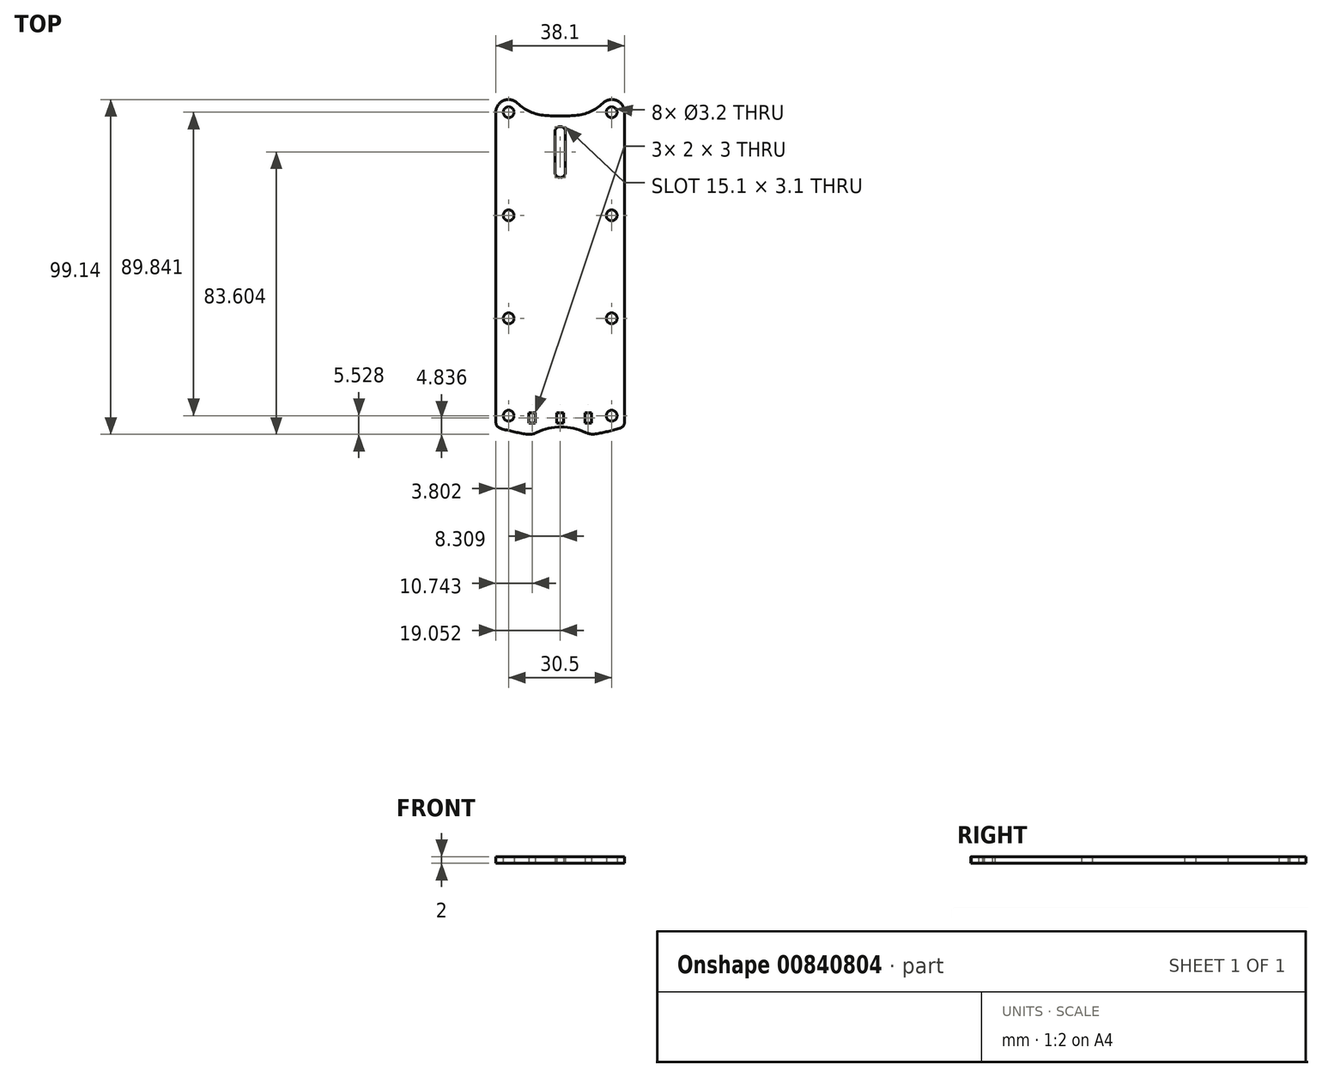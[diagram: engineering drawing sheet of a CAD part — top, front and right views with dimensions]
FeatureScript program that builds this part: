
annotation { "Feature Type Name" : "Feature", "Feature Type Description" : "" }
export const myFeature = defineFeature(function(context is Context, id is Id, definition is map)
    precondition{}
    {
        {
            var Q0;
            Q0=qCreatedBy(makeId("Top.planeOp"),FACE);
            var sketch = newSketch(context, id + "F0", { "sketchPlane" : qUnion([Q0])});
            skPoint(sketch, "E0.middle", {"position": v(-26.8, 6.98) * mm});
            skPoint(sketch, "E1.middle", {"position": v(-26.8, 51) * mm});
            skPoint(sketch, "E1.centerSnap0", {"position": v(-26.8, 26.98) * mm});
            skLineSegment(sketch, "E2.0", {"start": v(-45.86, 66.25) * mm, "end": v(-45.86, 60.43) * mm});
            skLineSegment(sketch, "E3", {"start": v(-7.76, 35.75) * mm, "end": v(-7.76, 5.25) * mm});
            skLineSegment(sketch, "E4.left", {"start": v(-45.86, 60.43) * mm, "end": v(-45.86, 5.25) * mm});
            skCircle(sketch, "E5", {"center": v(-11.56, 66.25) * mm, "radius": 1.6 * mm});
            skCircle(sketch, "E6", {"center": v(-42.06, 66.25) * mm, "radius": 1.6 * mm});
            skCircle(sketch, "E7", {"center": v(-42.06, 35.75) * mm, "radius": 1.6 * mm});
            skCircle(sketch, "E8", {"center": v(-11.56, 35.75) * mm, "radius": 1.6 * mm});
            skArc(sketch, "E9", {"start": v(-38.3, 66.25) * mm, "mid": v(-41.96, 70.02) * mm, "end": v(-45.85, 66.5) * mm});
            skArc(sketch, "E10.MirrorCS", {"start": v(-15.3, 66.25) * mm, "mid": v(-11.53, 70.02) * mm, "end": v(-7.76, 66.25) * mm});
            skPoint(sketch, "E11.middle", {"position": v(-26.8, -18.4) * mm});
            skLineSegment(sketch, "E12.bottom", {"start": v(-42.06, 35.75) * mm, "end": v(-40.46, 35.75) * mm});
            skCircle(sketch, "E13", {"center": v(-42.06, 5.25) * mm, "radius": 1.6 * mm});
            skCircle(sketch, "E14", {"center": v(-11.56, 5.25) * mm, "radius": 1.6 * mm});
            skLineSegment(sketch, "E15.trimOffspring", {"start": v(-13.16, 35.75) * mm, "end": v(-11.56, 35.75) * mm});
            skPoint(sketch, "E16.middle", {"position": v(-26.8, 42) * mm});
            skPoint(sketch, "E17", {"position": v(-26.8, 34.14) * mm});
            skPoint(sketch, "E17.positionSnap0", {"position": v(-26.8, 43.4) * mm});
            skLineSegment(sketch, "E18.bottom", {"start": v(-25.8, -22.78) * mm, "end": v(-27.8, -22.78) * mm});
            skLineSegment(sketch, "E18.top", {"start": v(-25.8, -25.78) * mm, "end": v(-27.8, -25.78) * mm});
            skLineSegment(sketch, "E18.left", {"start": v(-25.8, -22.78) * mm, "end": v(-25.8, -25.78) * mm});
            skLineSegment(sketch, "E18.right", {"start": v(-27.8, -22.78) * mm, "end": v(-27.8, -25.78) * mm});
            skPoint(sketch, "E18.middle", {"position": v(-26.8, -24.28) * mm});
            skPoint(sketch, "E18.middle.positionSnap0", {"position": v(-26.8, -20.66) * mm});
            skPoint(sketch, "E18.centerSnap0", {"position": v(-26.8, -20.66) * mm});
            skLineSegment(sketch, "E19.MirrorCS", {"start": v(-17.5, -22.78) * mm, "end": v(-17.5, -25.78) * mm});
            skLineSegment(sketch, "E20.MirrorCS", {"start": v(-19.5, -22.78) * mm, "end": v(-19.5, -25.78) * mm});
            skLineSegment(sketch, "E21.MirrorCS", {"start": v(-19.5, -25.78) * mm, "end": v(-17.5, -25.78) * mm});
            skPoint(sketch, "E22.MirrorP", {"position": v(-18.5, -24.28) * mm});
            skLineSegment(sketch, "E23.MirrorCS", {"start": v(-19.5, -22.78) * mm, "end": v(-17.5, -22.78) * mm});
            skLineSegment(sketch, "E24.MirrorCS", {"start": v(-36.12, -25.78) * mm, "end": v(-34.12, -25.78) * mm});
            skLineSegment(sketch, "E25.MirrorCS", {"start": v(-34.12, -22.78) * mm, "end": v(-34.12, -25.78) * mm});
            skLineSegment(sketch, "E26.MirrorCS", {"start": v(-36.12, -22.78) * mm, "end": v(-36.12, -25.78) * mm});
            skLineSegment(sketch, "E27.MirrorCS", {"start": v(-36.12, -22.78) * mm, "end": v(-34.12, -22.78) * mm});
            skPoint(sketch, "E28.MirrorP", {"position": v(-35.12, -24.28) * mm});
            skArc(sketch, "E29", {"start": v(-45.86, -26.92) * mm, "mid": v(-40.54, -28.35) * mm, "end": v(-35.12, -29.3) * mm});
            skArc(sketch, "E30", {"start": v(-18.02, -29.24) * mm, "mid": v(-26.58, -26.9) * mm, "end": v(-35.12, -29.3) * mm});
            skPoint(sketch, "E30.endSnap0", {"position": v(-35.12, -25.78) * mm});
            skArc(sketch, "E31.trimOffspring", {"start": v(-18.02, -29.24) * mm, "mid": v(-12.84, -28.3) * mm, "end": v(-7.76, -26.92) * mm});
            skCircle(sketch, "E32", {"center": v(-11.56, -23.6) * mm, "radius": 1.6 * mm});
            skCircle(sketch, "E33.MirrorC", {"center": v(-42.06, -23.6) * mm, "radius": 1.6 * mm});
            skLineSegment(sketch, "E34.MirrorCS", {"start": v(-40.46, 35.75) * mm, "end": v(-42.06, 35.75) * mm});
            skArc(sketch, "E35.MirrorCS", {"start": v(-38.3, 66.25) * mm, "mid": v(-42.08, 70.02) * mm, "end": v(-45.86, 66.25) * mm});
            skLineSegment(sketch, "E36.MirrorCS", {"start": v(-45.86, 35.75) * mm, "end": v(-45.86, 5.25) * mm});
            skLineSegment(sketch, "E37.MirrorCS", {"start": v(-42.06, 5.25) * mm, "end": v(-40.46, 5.25) * mm});
            skLineSegment(sketch, "E38.MirrorCS", {"start": v(-40.46, 5.25) * mm, "end": v(-42.06, 5.25) * mm});
            skPoint(sketch, "E39.MirrorP", {"position": v(-26.8, 14.02) * mm});
            skPoint(sketch, "E40.MirrorP", {"position": v(-26.8, 6.86) * mm});
            skLineSegment(sketch, "E41.MirrorCS", {"start": v(-13.16, 5.25) * mm, "end": v(-11.56, 5.25) * mm});
            skPoint(sketch, "E42.MirrorP", {"position": v(-26.8, 34.02) * mm});
            skPoint(sketch, "E43.MirrorP", {"position": v(-26.8, -1) * mm});
            skLineSegment(sketch, "E44.MirrorCS", {"start": v(-45.86, 5.25) * mm, "end": v(-45.86, 35.75) * mm});
            skLineSegment(sketch, "E45.MirrorCS", {"start": v(-45.86, -25.25) * mm, "end": v(-45.86, -19.44) * mm});
            skPoint(sketch, "E46.MirrorP", {"position": v(-26.8, -10) * mm});
            skPoint(sketch, "E47.MirrorP", {"position": v(-26.8, 1.74) * mm});
            skLineSegment(sketch, "E48.MirrorCS", {"start": v(-7.76, 5.25) * mm, "end": v(-7.76, 35.75) * mm});
            skLineSegment(sketch, "E49.MirrorCS", {"start": v(-20.33, 25.2) * mm, "end": v(-19.96, 24.68) * mm});
            skLineSegment(sketch, "E50.MirrorCS", {"start": v(-7.76, -25.25) * mm, "end": v(-7.76, -19.44) * mm});
            skLineSegment(sketch, "E51.MirrorCS", {"start": v(-33.29, 25.2) * mm, "end": v(-33.66, 24.68) * mm});
            skLineSegment(sketch, "E52.MirrorCS", {"start": v(-45.86, 5.25) * mm, "end": v(-45.86, 33.16) * mm});
            skLineSegment(sketch, "E53.trimOffspring", {"start": v(-45.86, -19.44) * mm, "end": v(-45.86, -26.92) * mm});
            skLineSegment(sketch, "E54.trimOffspring", {"start": v(-7.76, -19.44) * mm, "end": v(-7.76, -26.92) * mm});
            skLineSegment(sketch, "E55.trimOffspring", {"start": v(-7.76, 60.43) * mm, "end": v(-7.76, 66.42) * mm});
            skPoint(sketch, "E56.0.start.orphan", {"position": v(-7.76, 66.25) * mm});
            skLineSegment(sketch, "E57.trimOffspring", {"start": v(-45.86, 60.43) * mm, "end": v(-45.86, 66.25) * mm});
            skPoint(sketch, "E58.MirrorCS.start.orphan", {"position": v(-38.3, 66.25) * mm});
            skArc(sketch, "E59", {"start": v(-38.38, 65.51) * mm, "mid": v(-38.34, 65.88) * mm, "end": v(-38.3, 66.25) * mm});
            skPoint(sketch, "E60.visualSharp", {"position": v(-41.28, 56.57) * mm});
            skPoint(sketch, "E61.visualSharp", {"position": v(-49.55, 65.53) * mm});
            skPoint(sketch, "E62.visualSharp", {"position": v(-45.86, 66.25) * mm});
            skLineSegment(sketch, "E63.MirrorCS", {"start": v(-7.76, 66.25) * mm, "end": v(-7.76, 60.43) * mm});
            skLineSegment(sketch, "E64.MirrorCS", {"start": v(-7.76, 60.43) * mm, "end": v(-7.76, 66.25) * mm});
            skLineSegment(sketch, "E65.MirrorCS", {"start": v(-38.3, 43.4) * mm, "end": v(-36.8, 43.4) * mm});
            skArc(sketch, "E66.MirrorCS", {"start": v(-15.3, 66.25) * mm, "mid": v(-11.66, 70.02) * mm, "end": v(-7.77, 66.5) * mm});
            skPoint(sketch, "E67.MirrorP", {"position": v(-12.34, 56.57) * mm});
            skArc(sketch, "E68.MirrorCS", {"start": v(-15.23, 65.51) * mm, "mid": v(-15.27, 65.88) * mm, "end": v(-15.3, 66.25) * mm});
            skPoint(sketch, "E69.MirrorP", {"position": v(-15.3, 66.25) * mm});
            skLineSegment(sketch, "E70.MirrorCS", {"start": v(-15.3, 43.4) * mm, "end": v(-16.82, 43.4) * mm});
            skPoint(sketch, "E71.orphan", {"position": v(-41.28, 43.4) * mm});
            skLineSegment(sketch, "E72", {"start": v(-7.76, 60.43) * mm, "end": v(-7.76, -19.44) * mm});
            skLineSegment(sketch, "E73", {"start": v(-45.86, -19.44) * mm, "end": v(-45.86, 5.25) * mm});
            skArc(sketch, "E74", {"start": v(-38.3, 66.25) * mm, "mid": v(-26.8, 65.15) * mm, "end": v(-15.3, 66.25) * mm});
            skPoint(sketch, "E75", {"position": v(-26.8, 55.75) * mm});
            skPoint(sketch, "E76", {"position": v(-26.8, 54.48) * mm});
            skLineSegment(sketch, "E77.left", {"start": v(-25.26, 60.48) * mm, "end": v(-25.26, 48.48) * mm});
            skLineSegment(sketch, "E77.right", {"start": v(-28.36, 60.48) * mm, "end": v(-28.36, 48.48) * mm});
            skArc(sketch, "E78", {"start": v(-25.26, 60.48) * mm, "mid": v(-26.8, 62.03) * mm, "end": v(-28.36, 60.48) * mm});
            skArc(sketch, "E79", {"start": v(-28.36, 48.48) * mm, "mid": v(-26.8, 46.93) * mm, "end": v(-25.26, 48.48) * mm});
            skPoint(sketch, "E80.end.orphan", {"position": v(-36.8, 43.4) * mm});
            skLineSegment(sketch, "E81.trimOffspring", {"start": v(-36.8, 43.4) * mm, "end": v(-38.3, 43.4) * mm});
            skPoint(sketch, "E82.bottom.start.orphan", {"position": v(-15.8, 29.28) * mm});
            skPoint(sketch, "E82.right.start.orphan", {"position": v(-37.8, 29.28) * mm});
            skPoint(sketch, "E83.trimOffspring.end.orphan", {"position": v(-37.8, 24.68) * mm});
            skPoint(sketch, "E82.top.start.orphan", {"position": v(-15.8, 24.68) * mm});
            skPoint(sketch, "E11.right.start.orphan", {"position": v(-37.8, -16.16) * mm});
            skPoint(sketch, "E11.top.end.orphan", {"position": v(-37.8, -20.66) * mm});
            skPoint(sketch, "E11.left.end.orphan", {"position": v(-15.8, -20.66) * mm});
            skPoint(sketch, "E11.left.start.orphan", {"position": v(-15.8, -16.16) * mm});
            skSolve(sketch);
        }
        {
            var Q0;
            Q0 = qSketchRegion(id + "F0", true);
            var Q1;
            Q1=makeQuery(id+"F0.imprint","IMPRINT",FACE,{"disambiguationData":[TD([[makeQuery(id+"F0.imprint","IMPRINT",EDGE,{"derivedFrom":sQuery(id+"F0.wireOp",EDGE,"E4.left")}),1.0]])]});
            extrude(context, id + "F1", {"entities" : qUnion([Q0, Q1]), "depth" : 2 * mm, "offsetDistance" : 25 * mm});
        }
        {
            var Q0;
            Q0=makeQuery(id+"F1.opExtrude","SWEPT_EDGE",EDGE,{"disambiguationData":[OSD([sQuery(id+"F0.wireOp",EDGE,"E29"),sQuery(id+"F0.wireOp",EDGE,"E30")])]});
            var Q1;
            Q1=makeQuery(id+"F1.opExtrude","SWEPT_EDGE",EDGE,{"disambiguationData":[OSD([sQuery(id+"F0.wireOp",EDGE,"E30"),sQuery(id+"F0.wireOp",EDGE,"E31.trimOffspring")])]});
            fillet(context, id + "F2", {"entities" : qUnion([Q0, Q1]), "radius" : 5 * mm, "tangentPropagation" : true, "allowEdgeOverflow" : false});
        }
        {
            var Q0;
            Q0=makeQuery(id+"F1.opExtrude","SWEPT_EDGE",EDGE,{"disambiguationData":[OSD([sQuery(id+"F0.wireOp",EDGE,"E31.trimOffspring"),sQuery(id+"F0.wireOp",EDGE,"E54.trimOffspring")])]});
            var Q1;
            Q1=makeQuery(id+"F1.opExtrude","SWEPT_EDGE",EDGE,{"disambiguationData":[OSD([sQuery(id+"F0.wireOp",EDGE,"E29"),sQuery(id+"F0.wireOp",EDGE,"E53.trimOffspring")])]});
            fillet(context, id + "F3", {"entities" : qUnion([Q0, Q1]), "radius" : 2 * mm, "tangentPropagation" : true, "allowEdgeOverflow" : false});
        }
        {
            var Q0;
            Q0=makeQuery(id+"F1.opExtrude","SWEPT_EDGE",EDGE,{"disambiguationData":[OSD([sQuery(id+"F0.wireOp",EDGE,"E35.MirrorCS"),sQuery(id+"F0.wireOp",EDGE,"E74")])]});
            var Q1;
            Q1=makeQuery(id+"F1.opExtrude","SWEPT_EDGE",EDGE,{"disambiguationData":[OSD([sQuery(id+"F0.wireOp",EDGE,"E66.MirrorCS"),sQuery(id+"F0.wireOp",EDGE,"E74")])]});
            fillet(context, id + "F4", {"entities" : qUnion([Q0, Q1]), "radius" : 13.15 * mm, "tangentPropagation" : true, "allowEdgeOverflow" : false});
        }
    });
